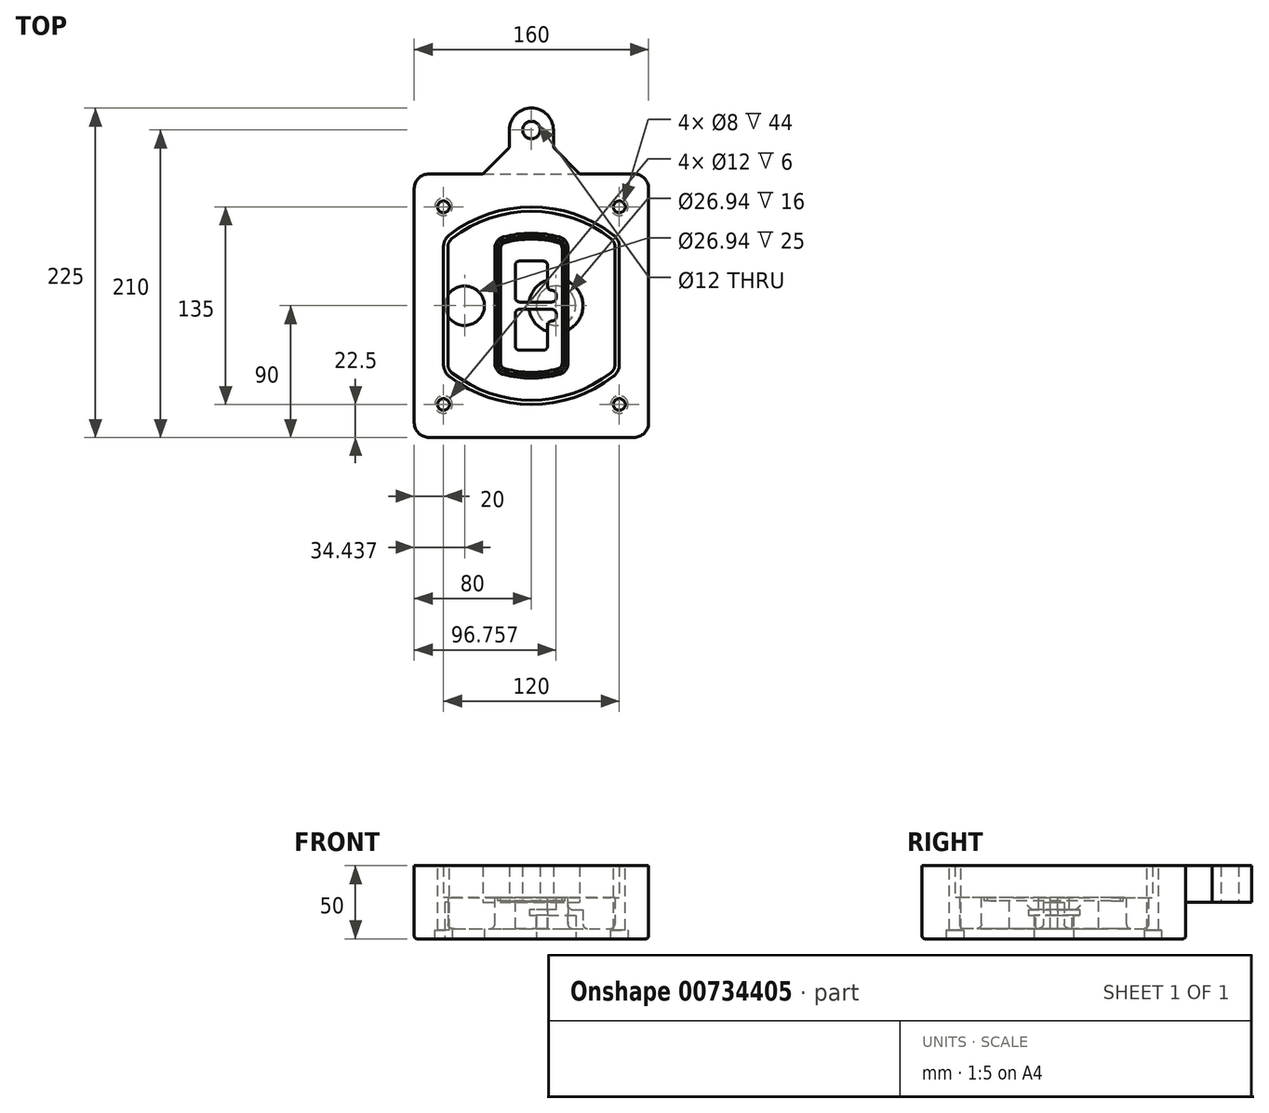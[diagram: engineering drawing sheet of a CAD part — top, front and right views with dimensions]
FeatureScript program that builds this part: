
annotation { "Feature Type Name" : "Feature", "Feature Type Description" : "" }
export const myFeature = defineFeature(function(context is Context, id is Id, definition is map)
    precondition{}
    {
        {
            var Q0;
            Q0=qCreatedBy(makeId("Top.planeOp"),FACE);
            var sketch = newSketch(context, id + "F0", { "sketchPlane" : qUnion([Q0])});
            skPoint(sketch, "E0.rect.middle", {"position": v(0, 0) * mm});
            skLineSegment(sketch, "E1.bottom", {"start": v(-70, -90) * mm, "end": v(70, -90) * mm});
            skLineSegment(sketch, "E1.top", {"start": v(-70, 90) * mm, "end": v(70, 90) * mm});
            skLineSegment(sketch, "E1.left", {"start": v(-80, -80) * mm, "end": v(-80, 80) * mm});
            skLineSegment(sketch, "E1.right", {"start": v(80, -80) * mm, "end": v(80, 80) * mm});
            skLineSegment(sketch, "E2", {"start": v(-80, 90) * mm, "end": v(80, -90) * mm, "construction": true});
            skLineSegment(sketch, "E3", {"start": v(80, 90) * mm, "end": v(-80, -90) * mm, "construction": true});
            skCircle(sketch, "E4", {"center": v(-60, 67.5) * mm, "radius": 4 * mm});
            skCircle(sketch, "E5", {"center": v(60, 67.5) * mm, "radius": 4 * mm});
            skCircle(sketch, "E6", {"center": v(60, -67.5) * mm, "radius": 4 * mm});
            skCircle(sketch, "E7", {"center": v(-60, -67.5) * mm, "radius": 4 * mm});
            skLineSegment(sketch, "E8", {"start": v(-60, 67.5) * mm, "end": v(60, 67.5) * mm, "construction": true});
            skLineSegment(sketch, "E9", {"start": v(60, 67.5) * mm, "end": v(60, -67.5) * mm, "construction": true});
            skLineSegment(sketch, "E10", {"start": v(60, -67.5) * mm, "end": v(-60, -67.5) * mm, "construction": true});
            skLineSegment(sketch, "E11", {"start": v(-60, -67.5) * mm, "end": v(-60, 67.5) * mm, "construction": true});
            skLineSegment(sketch, "E12", {"start": v(-60, 40.3) * mm, "end": v(-60, -40.3) * mm});
            skLineSegment(sketch, "E13", {"start": v(60, 40.3) * mm, "end": v(60, -40.3) * mm});
            skArc(sketch, "E14", {"start": v(56.15, 48.18) * mm, "mid": v(0, 67.5) * mm, "end": v(-56.15, 48.18) * mm});
            skArc(sketch, "E15", {"start": v(-56.15, -48.18) * mm, "mid": v(0, -67.5) * mm, "end": v(56.15, -48.18) * mm});
            skLineSegment(sketch, "E16", {"start": v(-60, 0) * mm, "end": v(60, 0) * mm, "construction": true});
            skPoint(sketch, "E17.visualSharp", {"position": v(-60, -45) * mm});
            skArc(sketch, "E17.filletArc", {"start": v(-60, -40.3) * mm, "mid": v(-58.99, -44.68) * mm, "end": v(-56.15, -48.18) * mm});
            skPoint(sketch, "E18.visualSharp", {"position": v(-60, 45) * mm});
            skArc(sketch, "E18.filletArc", {"start": v(-56.15, 48.18) * mm, "mid": v(-58.99, 44.68) * mm, "end": v(-60, 40.3) * mm});
            skPoint(sketch, "E19.visualSharp", {"position": v(60, 45) * mm});
            skArc(sketch, "E19.filletArc", {"start": v(60, 40.3) * mm, "mid": v(58.99, 44.68) * mm, "end": v(56.15, 48.18) * mm});
            skPoint(sketch, "E20.visualSharp", {"position": v(60, -45) * mm});
            skArc(sketch, "E20.filletArc", {"start": v(56.15, -48.18) * mm, "mid": v(58.99, -44.68) * mm, "end": v(60, -40.3) * mm});
            skPoint(sketch, "E21.visualSharp", {"position": v(-80, 90) * mm});
            skArc(sketch, "E21.filletArc", {"start": v(-70, 90) * mm, "mid": v(-77.07, 87.07) * mm, "end": v(-80, 80) * mm});
            skPoint(sketch, "E22.visualSharp", {"position": v(80, 90) * mm});
            skArc(sketch, "E22.filletArc", {"start": v(80, 80) * mm, "mid": v(77.07, 87.07) * mm, "end": v(70, 90) * mm});
            skPoint(sketch, "E23.visualSharp", {"position": v(80, -90) * mm});
            skArc(sketch, "E23.filletArc", {"start": v(70, -90) * mm, "mid": v(77.07, -87.07) * mm, "end": v(80, -80) * mm});
            skPoint(sketch, "E24.visualSharp", {"position": v(-80, -90) * mm});
            skArc(sketch, "E24.filletArc", {"start": v(-80, -80) * mm, "mid": v(-77.07, -87.07) * mm, "end": v(-70, -90) * mm});
            skArc(sketch, "E25.0", {"start": v(57, 40.3) * mm, "mid": v(56.3, 43.36) * mm, "end": v(54.3, 45.81) * mm});
            skLineSegment(sketch, "E25.1", {"start": v(57, 40.3) * mm, "end": v(57, -40.3) * mm});
            skArc(sketch, "E25.2", {"start": v(54.3, -45.81) * mm, "mid": v(56.3, -43.36) * mm, "end": v(57, -40.3) * mm});
            skArc(sketch, "E25.3", {"start": v(-54.3, -45.81) * mm, "mid": v(0, -64.5) * mm, "end": v(54.3, -45.81) * mm});
            skArc(sketch, "E25.4", {"start": v(-57, -40.3) * mm, "mid": v(-56.3, -43.36) * mm, "end": v(-54.3, -45.81) * mm});
            skArc(sketch, "E25.5", {"start": v(54.3, 45.81) * mm, "mid": v(0, 64.5) * mm, "end": v(-54.3, 45.81) * mm});
            skLineSegment(sketch, "E25.6", {"start": v(-57, 40.3) * mm, "end": v(-57, -40.3) * mm});
            skArc(sketch, "E25.7", {"start": v(-54.3, 45.81) * mm, "mid": v(-56.3, 43.36) * mm, "end": v(-57, 40.3) * mm});
            skArc(sketch, "E26.0", {"start": v(-58.62, 51.33) * mm, "mid": v(-62.58, 46.43) * mm, "end": v(-64, 40.3) * mm});
            skArc(sketch, "E26.1", {"start": v(58.62, 51.33) * mm, "mid": v(0, 71.5) * mm, "end": v(-58.62, 51.33) * mm});
            skArc(sketch, "E26.2", {"start": v(64, 40.3) * mm, "mid": v(62.58, 46.43) * mm, "end": v(58.62, 51.33) * mm});
            skLineSegment(sketch, "E26.3", {"start": v(64, 40.3) * mm, "end": v(64, -40.3) * mm});
            skArc(sketch, "E26.4", {"start": v(58.62, -51.33) * mm, "mid": v(62.58, -46.43) * mm, "end": v(64, -40.3) * mm});
            skLineSegment(sketch, "E26.5", {"start": v(-64, 40.3) * mm, "end": v(-64, -40.3) * mm});
            skArc(sketch, "E26.6", {"start": v(-58.62, -51.33) * mm, "mid": v(0, -71.5) * mm, "end": v(58.62, -51.33) * mm});
            skArc(sketch, "E26.7", {"start": v(-64, -40.3) * mm, "mid": v(-62.58, -46.43) * mm, "end": v(-58.62, -51.33) * mm});
            skSolve(sketch);
        }
        {
            var Q0;
            Q0=makeQuery(id+"F0.imprint","IMPRINT",FACE,{"disambiguationData":[TD([[makeQuery(id+"F0.imprint","IMPRINT",EDGE,{"derivedFrom":sQuery(id+"F0.wireOp",EDGE,"E1.bottom")}),1.0]])]});
            var Q1;
            Q1=makeQuery(id+"F0.imprint","IMPRINT",FACE,{"disambiguationData":[TD([[makeQuery(id+"F0.imprint","IMPRINT",EDGE,{"derivedFrom":sQuery(id+"F0.wireOp",EDGE,"E12")}),1.0]])]});
            var Q2;
            Q2=makeQuery(id+"F0.imprint","IMPRINT",FACE,{"disambiguationData":[TD([[makeQuery(id+"F0.imprint","IMPRINT",EDGE,{"derivedFrom":sQuery(id+"F0.wireOp",EDGE,"E25.0")}),1.0]])]});
            var Q3;
            Q3=makeQuery(id+"F0.imprint","IMPRINT",FACE,{"disambiguationData":[TD([[makeQuery(id+"F0.imprint","IMPRINT",EDGE,{"derivedFrom":sQuery(id+"F0.wireOp",EDGE,"E12")}),-1.0]])]});
            extrude(context, id + "F1", {"entities" : qUnion([Q0, Q1, Q2, Q3]), "oppositeDirection" : true, "depth" : 25 * mm});
        }
        {
            var Q0;
            Q0=makeQuery(id+"F0.imprint","IMPRINT",FACE,{"disambiguationData":[TD([[makeQuery(id+"F0.imprint","IMPRINT",EDGE,{"derivedFrom":sQuery(id+"F0.wireOp",EDGE,"E12")}),1.0]])]});
            extrude(context, id + "F2", {"entities" : qUnion([Q0]), "operationType" : NewBodyOperationType.ADD, "depth" : 3 * mm});
        }
        {
            var Q0;
            Q0=makeQuery(id+"F0.imprint","IMPRINT",FACE,{"disambiguationData":[TD([[makeQuery(id+"F0.imprint","IMPRINT",EDGE,{"derivedFrom":sQuery(id+"F0.wireOp",EDGE,"E25.0")}),1.0]])]});
            extrude(context, id + "F3", {"entities" : qUnion([Q0]), "operationType" : NewBodyOperationType.REMOVE, "oppositeDirection" : true, "depth" : 18 * mm});
        }
        {
            var Q0;
            Q0=makeQuery(id+"F2.opExtrude","CAP_FACE",FACE,{"disambiguationData":[OSD([sQuery(id+"F0.wireOp",EDGE,"E12"),sQuery(id+"F0.wireOp",EDGE,"E13"),sQuery(id+"F0.wireOp",EDGE,"E14"),sQuery(id+"F0.wireOp",EDGE,"E15"),sQuery(id+"F0.wireOp",EDGE,"E17.filletArc"),sQuery(id+"F0.wireOp",EDGE,"E18.filletArc"),sQuery(id+"F0.wireOp",EDGE,"E19.filletArc"),sQuery(id+"F0.wireOp",EDGE,"E20.filletArc"),sQuery(id+"F0.wireOp",EDGE,"E25.0"),sQuery(id+"F0.wireOp",EDGE,"E25.1"),sQuery(id+"F0.wireOp",EDGE,"E25.2"),sQuery(id+"F0.wireOp",EDGE,"E25.3"),sQuery(id+"F0.wireOp",EDGE,"E25.4"),sQuery(id+"F0.wireOp",EDGE,"E25.5"),sQuery(id+"F0.wireOp",EDGE,"E25.6"),sQuery(id+"F0.wireOp",EDGE,"E25.7")])],"isStart":false});
            var sketch = newSketch(context, id + "F4", { "sketchPlane" : qUnion([Q0])});
            skArc(sketch, "E27.0", {"start": v(-19.08, -46.97) * mm, "mid": v(0, -49.5) * mm, "end": v(19.08, -46.97) * mm});
            skArc(sketch, "E28.0", {"start": v(19.08, 46.97) * mm, "mid": v(0, 49.5) * mm, "end": v(-19.08, 46.97) * mm});
            skLineSegment(sketch, "E29", {"start": v(-25, 39.25) * mm, "end": v(-25, -39.25) * mm});
            skLineSegment(sketch, "E30", {"start": v(25, 39.25) * mm, "end": v(25, -39.25) * mm});
            skLineSegment(sketch, "E31", {"start": v(-25, 45.1) * mm, "end": v(25, 45.1) * mm, "construction": true});
            skLineSegment(sketch, "E32", {"start": v(-25, -45.1) * mm, "end": v(25, -45.1) * mm, "construction": true});
            skPoint(sketch, "E33.visualSharp", {"position": v(-25, 45.1) * mm});
            skArc(sketch, "E33.filletArc", {"start": v(-19.08, 46.97) * mm, "mid": v(-23.35, 44.11) * mm, "end": v(-25, 39.25) * mm});
            skPoint(sketch, "E34.visualSharp", {"position": v(25, 45.1) * mm});
            skArc(sketch, "E34.filletArc", {"start": v(25, 39.25) * mm, "mid": v(23.35, 44.11) * mm, "end": v(19.08, 46.97) * mm});
            skPoint(sketch, "E35.visualSharp", {"position": v(25, -45.1) * mm});
            skArc(sketch, "E35.filletArc", {"start": v(19.08, -46.97) * mm, "mid": v(23.35, -44.11) * mm, "end": v(25, -39.25) * mm});
            skPoint(sketch, "E36.visualSharp", {"position": v(-25, -45.1) * mm});
            skArc(sketch, "E36.filletArc", {"start": v(-25, -39.25) * mm, "mid": v(-23.35, -44.11) * mm, "end": v(-19.08, -46.97) * mm});
            skArc(sketch, "E37.0", {"start": v(54.3, 45.81) * mm, "mid": v(0, 64.5) * mm, "end": v(-54.3, 45.81) * mm});
            skArc(sketch, "E37.1", {"start": v(-54.3, 45.81) * mm, "mid": v(-56.3, 43.36) * mm, "end": v(-57, 40.3) * mm});
            skLineSegment(sketch, "E37.2", {"start": v(-57, 40.3) * mm, "end": v(-57, -40.3) * mm});
            skArc(sketch, "E37.3", {"start": v(-57, -40.3) * mm, "mid": v(-56.3, -43.36) * mm, "end": v(-54.3, -45.81) * mm});
            skArc(sketch, "E37.4", {"start": v(-54.3, -45.81) * mm, "mid": v(0, -64.5) * mm, "end": v(54.3, -45.81) * mm});
            skArc(sketch, "E37.5", {"start": v(54.3, -45.81) * mm, "mid": v(56.3, -43.36) * mm, "end": v(57, -40.3) * mm});
            skLineSegment(sketch, "E37.6", {"start": v(57, 40.3) * mm, "end": v(57, -40.3) * mm});
            skArc(sketch, "E37.7", {"start": v(57, 40.3) * mm, "mid": v(56.3, 43.36) * mm, "end": v(54.3, 45.81) * mm});
            skLineSegment(sketch, "E38.0", {"start": v(23, 39.25) * mm, "end": v(23, -39.25) * mm});
            skArc(sketch, "E38.1", {"start": v(18.56, -45.04) * mm, "mid": v(21.76, -42.9) * mm, "end": v(23, -39.25) * mm});
            skArc(sketch, "E38.2", {"start": v(-18.56, -45.04) * mm, "mid": v(0, -47.5) * mm, "end": v(18.56, -45.04) * mm});
            skArc(sketch, "E38.3", {"start": v(-23, -39.25) * mm, "mid": v(-21.76, -42.9) * mm, "end": v(-18.56, -45.04) * mm});
            skLineSegment(sketch, "E38.4", {"start": v(-23, 39.25) * mm, "end": v(-23, -39.25) * mm});
            skArc(sketch, "E38.5", {"start": v(23, 39.25) * mm, "mid": v(21.76, 42.9) * mm, "end": v(18.56, 45.04) * mm});
            skArc(sketch, "E38.6", {"start": v(-18.56, 45.04) * mm, "mid": v(-21.76, 42.9) * mm, "end": v(-23, 39.25) * mm});
            skArc(sketch, "E38.7", {"start": v(18.56, 45.04) * mm, "mid": v(0, 47.5) * mm, "end": v(-18.56, 45.04) * mm});
            skArc(sketch, "E39.0", {"start": v(21, 39.25) * mm, "mid": v(20.18, 41.68) * mm, "end": v(18.04, 43.1) * mm});
            skLineSegment(sketch, "E39.1", {"start": v(21, 39.25) * mm, "end": v(21, -39.25) * mm});
            skArc(sketch, "E39.2", {"start": v(18.04, -43.1) * mm, "mid": v(20.18, -41.68) * mm, "end": v(21, -39.25) * mm});
            skArc(sketch, "E39.3", {"start": v(-18.04, -43.1) * mm, "mid": v(0, -45.5) * mm, "end": v(18.04, -43.1) * mm});
            skArc(sketch, "E39.4", {"start": v(-21, -39.25) * mm, "mid": v(-20.18, -41.68) * mm, "end": v(-18.04, -43.1) * mm});
            skArc(sketch, "E39.5", {"start": v(18.04, 43.1) * mm, "mid": v(0, 45.5) * mm, "end": v(-18.04, 43.1) * mm});
            skLineSegment(sketch, "E39.6", {"start": v(-21, 39.25) * mm, "end": v(-21, -39.25) * mm});
            skArc(sketch, "E39.7", {"start": v(-18.04, 43.1) * mm, "mid": v(-20.18, 41.68) * mm, "end": v(-21, 39.25) * mm});
            skLineSegment(sketch, "E40", {"start": v(-25, 0) * mm, "end": v(25, 0) * mm, "construction": true});
            skLineSegment(sketch, "E41", {"start": v(-11, 5.5) * mm, "end": v(-11, 27.5) * mm});
            skLineSegment(sketch, "E42", {"start": v(-8, 30.5) * mm, "end": v(8, 30.5) * mm});
            skLineSegment(sketch, "E43", {"start": v(11, 27.5) * mm, "end": v(11, 13.5) * mm});
            skLineSegment(sketch, "E44", {"start": v(14, 10.5) * mm, "end": v(14, 10.5) * mm});
            skLineSegment(sketch, "E45", {"start": v(17, 7.5) * mm, "end": v(17, 5.5) * mm});
            skLineSegment(sketch, "E46", {"start": v(14, 2.5) * mm, "end": v(-8, 2.5) * mm});
            skPoint(sketch, "E47.visualSharp", {"position": v(-11, 30.5) * mm});
            skArc(sketch, "E47.filletArc", {"start": v(-8, 30.5) * mm, "mid": v(-10.12, 29.62) * mm, "end": v(-11, 27.5) * mm});
            skPoint(sketch, "E48.visualSharp", {"position": v(11, 30.5) * mm});
            skArc(sketch, "E48.filletArc", {"start": v(11, 27.5) * mm, "mid": v(10.12, 29.62) * mm, "end": v(8, 30.5) * mm});
            skPoint(sketch, "E49.visualSharp", {"position": v(11, 10.5) * mm});
            skArc(sketch, "E49.filletArc", {"start": v(11, 13.5) * mm, "mid": v(11.88, 11.38) * mm, "end": v(14, 10.5) * mm});
            skPoint(sketch, "E50.visualSharp", {"position": v(17, 10.5) * mm});
            skArc(sketch, "E50.filletArc", {"start": v(17, 7.5) * mm, "mid": v(16.12, 9.62) * mm, "end": v(14, 10.5) * mm});
            skPoint(sketch, "E51.visualSharp", {"position": v(17, 2.5) * mm});
            skArc(sketch, "E51.filletArc", {"start": v(14, 2.5) * mm, "mid": v(16.12, 3.38) * mm, "end": v(17, 5.5) * mm});
            skPoint(sketch, "E52.visualSharp", {"position": v(-11, 2.5) * mm});
            skArc(sketch, "E52.filletArc", {"start": v(-11, 5.5) * mm, "mid": v(-10.12, 3.38) * mm, "end": v(-8, 2.5) * mm});
            skLineSegment(sketch, "E53.0.MirrorCS", {"start": v(14, -2.5) * mm, "end": v(-8, -2.5) * mm});
            skArc(sketch, "E54.0.MirrorCS", {"start": v(-11, -5.5) * mm, "mid": v(-10.12, -3.38) * mm, "end": v(-8, -2.5) * mm});
            skLineSegment(sketch, "E55.0.MirrorCS", {"start": v(-11, -5.5) * mm, "end": v(-11, -27.5) * mm});
            skArc(sketch, "E56.0.MirrorCS", {"start": v(-8, -30.5) * mm, "mid": v(-10.12, -29.62) * mm, "end": v(-11, -27.5) * mm});
            skLineSegment(sketch, "E57.0.MirrorCS", {"start": v(-8, -30.5) * mm, "end": v(8, -30.5) * mm});
            skArc(sketch, "E58.0.MirrorCS", {"start": v(11, -27.5) * mm, "mid": v(10.12, -29.62) * mm, "end": v(8, -30.5) * mm});
            skLineSegment(sketch, "E59.0.MirrorCS", {"start": v(11, -27.5) * mm, "end": v(11, -13.5) * mm});
            skArc(sketch, "E60.0.MirrorCS", {"start": v(11, -13.5) * mm, "mid": v(11.88, -11.38) * mm, "end": v(14, -10.5) * mm});
            skArc(sketch, "E61.0.MirrorCS", {"start": v(17, -7.5) * mm, "mid": v(16.12, -9.62) * mm, "end": v(14, -10.5) * mm});
            skLineSegment(sketch, "E62.0.MirrorCS", {"start": v(17, -7.5) * mm, "end": v(17, -5.5) * mm});
            skArc(sketch, "E63.0.MirrorCS", {"start": v(14, -2.5) * mm, "mid": v(16.12, -3.38) * mm, "end": v(17, -5.5) * mm});
            skSolve(sketch);
        }
        {
            var Q0;
            Q0=makeQuery(id+"F4.imprint","IMPRINT",FACE,{"disambiguationData":[TD([[makeQuery(id+"F4.imprint","IMPRINT",EDGE,{"derivedFrom":sQuery(id+"F4.wireOp",EDGE,"E27.0")}),1.0]])]});
            var Q1;
            Q1=makeQuery(id+"F4.imprint","IMPRINT",FACE,{"disambiguationData":[TD([[makeQuery(id+"F4.imprint","IMPRINT",EDGE,{"derivedFrom":sQuery(id+"F4.wireOp",EDGE,"E38.0")}),-1.0]])]});
            var Q2;
            Q2=makeQuery(id+"F4.imprint","IMPRINT",FACE,{"disambiguationData":[TD([[makeQuery(id+"F4.imprint","IMPRINT",EDGE,{"derivedFrom":sQuery(id+"F4.wireOp",EDGE,"E39.0")}),1.0]])]});
            extrude(context, id + "F5", {"entities" : qUnion([Q0, Q1, Q2]), "operationType" : NewBodyOperationType.ADD, "endBound" : BoundingType.UP_TO_NEXT, "oppositeDirection" : true, "depth" : 25 * mm});
        }
        {
            var Q0;
            Q0=makeQuery(id+"F4.imprint","IMPRINT",FACE,{"disambiguationData":[TD([[makeQuery(id+"F4.imprint","IMPRINT",EDGE,{"derivedFrom":sQuery(id+"F4.wireOp",EDGE,"E38.0")}),-1.0]])]});
            extrude(context, id + "F6", {"entities" : qUnion([Q0]), "operationType" : NewBodyOperationType.REMOVE, "oppositeDirection" : true, "depth" : 2 * mm});
        }
        {
            var Q0;
            Q0=makeQuery(id+"F1.opExtrude","CAP_FACE",FACE,{"disambiguationData":[OSD([sQuery(id+"F0.wireOp",EDGE,"E1.bottom"),sQuery(id+"F0.wireOp",EDGE,"E1.top"),sQuery(id+"F0.wireOp",EDGE,"E1.left"),sQuery(id+"F0.wireOp",EDGE,"E1.right"),sQuery(id+"F0.wireOp",EDGE,"E4"),sQuery(id+"F0.wireOp",EDGE,"E5"),sQuery(id+"F0.wireOp",EDGE,"E6"),sQuery(id+"F0.wireOp",EDGE,"E7"),sQuery(id+"F0.wireOp",EDGE,"E21.filletArc"),sQuery(id+"F0.wireOp",EDGE,"E22.filletArc"),sQuery(id+"F0.wireOp",EDGE,"E23.filletArc"),sQuery(id+"F0.wireOp",EDGE,"E24.filletArc")])],"isStart":false});
            var sketch = newSketch(context, id + "F7", { "sketchPlane" : qUnion([Q0])});
            skCircle(sketch, "E64", {"center": v(16.76, 0) * mm, "radius": 13.47 * mm});
            skCircle(sketch, "E65", {"center": v(-45.56, 0) * mm, "radius": 13.47 * mm});
            skLineSegment(sketch, "E66", {"start": v(80, 0) * mm, "end": v(-80, 0) * mm});
            skCircle(sketch, "E67", {"center": v(16.76, 0) * mm, "radius": 18.47 * mm});
            skCircle(sketch, "E68", {"center": v(60, -67.5) * mm, "radius": 6 * mm});
            skCircle(sketch, "E69", {"center": v(-60, -67.5) * mm, "radius": 6 * mm});
            skCircle(sketch, "E70", {"center": v(-60, 67.5) * mm, "radius": 6 * mm});
            skCircle(sketch, "E71", {"center": v(60, 67.5) * mm, "radius": 6 * mm});
            skSolve(sketch);
        }
        {
            var Q0;
            {var subQ1=sQuery(id+"F7.wireOp",EDGE,"E66");var subQ4=sQuery(id+"F7.wireOp",EDGE,"E64");var subQ6=makeQuery(id+"F7.imprint","INTERSECT",VERTEX,{"disambiguationData":[OD(0.0)],"derivedFrom":[subQ4,subQ1]});Q0=makeQuery(id+"F7.imprint","IMPRINT",FACE,{"disambiguationData":[TD([[makeQuery(id+"F7.imprint","IMPRINT",EDGE,{"disambiguationData":[TD([[subQ6,-1.0]])],"derivedFrom":subQ4}),-1.0]])]});}
            var Q1;
            {var subQ0=sQuery(id+"F7.wireOp",EDGE,"E66");var subQ1=sQuery(id+"F7.wireOp",EDGE,"E64");var subQ3=makeQuery(id+"F7.imprint","INTERSECT",VERTEX,{"disambiguationData":[OD(0.0)],"derivedFrom":[subQ1,subQ0]});Q1=makeQuery(id+"F7.imprint","IMPRINT",FACE,{"disambiguationData":[TD([[makeQuery(id+"F7.imprint","IMPRINT",EDGE,{"disambiguationData":[TD([[subQ3,-1.0]])],"derivedFrom":subQ1}),1.0]])]});}
            var Q2;
            {var subQ0=sQuery(id+"F7.wireOp",EDGE,"E66");var subQ1=sQuery(id+"F7.wireOp",EDGE,"E64");var subQ3=makeQuery(id+"F7.imprint","INTERSECT",VERTEX,{"disambiguationData":[OD(0.0)],"derivedFrom":[subQ1,subQ0]});Q2=makeQuery(id+"F7.imprint","IMPRINT",FACE,{"disambiguationData":[TD([[makeQuery(id+"F7.imprint","IMPRINT",EDGE,{"disambiguationData":[TD([[subQ3,1.0]])],"derivedFrom":subQ1}),1.0]])]});}
            var Q3;
            {var subQ1=sQuery(id+"F7.wireOp",EDGE,"E66");var subQ4=sQuery(id+"F7.wireOp",EDGE,"E64");var subQ6=makeQuery(id+"F7.imprint","INTERSECT",VERTEX,{"disambiguationData":[OD(0.0)],"derivedFrom":[subQ4,subQ1]});Q3=makeQuery(id+"F7.imprint","IMPRINT",FACE,{"disambiguationData":[TD([[makeQuery(id+"F7.imprint","IMPRINT",EDGE,{"disambiguationData":[TD([[subQ6,1.0]])],"derivedFrom":subQ4}),-1.0]])]});}
            extrude(context, id + "F8", {"entities" : qUnion([Q0, Q1, Q2, Q3]), "operationType" : NewBodyOperationType.ADD, "oppositeDirection" : true, "depth" : 20 * mm});
        }
        {
            var Q0;
            {var subQ0=sQuery(id+"F7.wireOp",EDGE,"E66");var subQ1=sQuery(id+"F7.wireOp",EDGE,"E64");var subQ3=makeQuery(id+"F7.imprint","INTERSECT",VERTEX,{"disambiguationData":[OD(0.0)],"derivedFrom":[subQ1,subQ0]});Q0=makeQuery(id+"F7.imprint","IMPRINT",FACE,{"disambiguationData":[TD([[makeQuery(id+"F7.imprint","IMPRINT",EDGE,{"disambiguationData":[TD([[subQ3,-1.0]])],"derivedFrom":subQ1}),1.0]])]});}
            var Q1;
            {var subQ0=sQuery(id+"F7.wireOp",EDGE,"E66");var subQ1=sQuery(id+"F7.wireOp",EDGE,"E64");var subQ3=makeQuery(id+"F7.imprint","INTERSECT",VERTEX,{"disambiguationData":[OD(0.0)],"derivedFrom":[subQ1,subQ0]});Q1=makeQuery(id+"F7.imprint","IMPRINT",FACE,{"disambiguationData":[TD([[makeQuery(id+"F7.imprint","IMPRINT",EDGE,{"disambiguationData":[TD([[subQ3,1.0]])],"derivedFrom":subQ1}),1.0]])]});}
            extrude(context, id + "F9", {"entities" : qUnion([Q0, Q1]), "operationType" : NewBodyOperationType.REMOVE, "oppositeDirection" : true, "depth" : 16 * mm});
        }
        {
            var Q0;
            {var subQ0=sQuery(id+"F7.wireOp",EDGE,"E66");var subQ1=sQuery(id+"F7.wireOp",EDGE,"E65");var subQ3=makeQuery(id+"F7.imprint","INTERSECT",VERTEX,{"disambiguationData":[OD(0.0)],"derivedFrom":[subQ1,subQ0]});Q0=makeQuery(id+"F7.imprint","IMPRINT",FACE,{"disambiguationData":[TD([[makeQuery(id+"F7.imprint","IMPRINT",EDGE,{"disambiguationData":[TD([[subQ3,-1.0]])],"derivedFrom":subQ1}),1.0]])]});}
            var Q1;
            {var subQ0=sQuery(id+"F7.wireOp",EDGE,"E66");var subQ1=sQuery(id+"F7.wireOp",EDGE,"E65");var subQ3=makeQuery(id+"F7.imprint","INTERSECT",VERTEX,{"disambiguationData":[OD(0.0)],"derivedFrom":[subQ1,subQ0]});Q1=makeQuery(id+"F7.imprint","IMPRINT",FACE,{"disambiguationData":[TD([[makeQuery(id+"F7.imprint","IMPRINT",EDGE,{"disambiguationData":[TD([[subQ3,1.0]])],"derivedFrom":subQ1}),1.0]])]});}
            extrude(context, id + "F10", {"entities" : qUnion([Q0, Q1]), "operationType" : NewBodyOperationType.REMOVE, "oppositeDirection" : true, "depth" : 25 * mm});
        }
        {
            var Q0;
            Q0=makeQuery(id+"F7.imprint","IMPRINT",FACE,{"disambiguationData":[TD([[makeQuery(id+"F7.imprint","IMPRINT",EDGE,{"derivedFrom":sQuery(id+"F7.wireOp",EDGE,"E68")}),1.0]])]});
            var Q1;
            Q1=makeQuery(id+"F7.imprint","IMPRINT",FACE,{"disambiguationData":[TD([[makeQuery(id+"F7.imprint","IMPRINT",EDGE,{"derivedFrom":makeQuery(id+"F1.opExtrude","CAP_EDGE",EDGE,{"disambiguationData":[OSD([sQuery(id+"F0.wireOp",EDGE,"E5")])],"isStart":false})}),-1.0]])]});
            var Q2;
            Q2=makeQuery(id+"F7.imprint","IMPRINT",FACE,{"disambiguationData":[TD([[makeQuery(id+"F7.imprint","IMPRINT",EDGE,{"derivedFrom":sQuery(id+"F7.wireOp",EDGE,"E69")}),1.0]])]});
            var Q3;
            Q3=makeQuery(id+"F7.imprint","IMPRINT",FACE,{"disambiguationData":[TD([[makeQuery(id+"F7.imprint","IMPRINT",EDGE,{"derivedFrom":makeQuery(id+"F1.opExtrude","CAP_EDGE",EDGE,{"disambiguationData":[OSD([sQuery(id+"F0.wireOp",EDGE,"E4")])],"isStart":false})}),-1.0]])]});
            var Q4;
            Q4=makeQuery(id+"F7.imprint","IMPRINT",FACE,{"disambiguationData":[TD([[makeQuery(id+"F7.imprint","IMPRINT",EDGE,{"derivedFrom":sQuery(id+"F7.wireOp",EDGE,"E70")}),1.0]])]});
            var Q5;
            Q5=makeQuery(id+"F7.imprint","IMPRINT",FACE,{"disambiguationData":[TD([[makeQuery(id+"F7.imprint","IMPRINT",EDGE,{"derivedFrom":makeQuery(id+"F1.opExtrude","CAP_EDGE",EDGE,{"disambiguationData":[OSD([sQuery(id+"F0.wireOp",EDGE,"E7")])],"isStart":false})}),-1.0]])]});
            var Q6;
            Q6=makeQuery(id+"F7.imprint","IMPRINT",FACE,{"disambiguationData":[TD([[makeQuery(id+"F7.imprint","IMPRINT",EDGE,{"derivedFrom":sQuery(id+"F7.wireOp",EDGE,"E71")}),1.0]])]});
            var Q7;
            Q7=makeQuery(id+"F7.imprint","IMPRINT",FACE,{"disambiguationData":[TD([[makeQuery(id+"F7.imprint","IMPRINT",EDGE,{"derivedFrom":makeQuery(id+"F1.opExtrude","CAP_EDGE",EDGE,{"disambiguationData":[OSD([sQuery(id+"F0.wireOp",EDGE,"E6")])],"isStart":false})}),-1.0]])]});
            extrude(context, id + "F11", {"entities" : qUnion([Q0, Q1, Q2, Q3, Q4, Q5, Q6, Q7]), "operationType" : NewBodyOperationType.REMOVE, "oppositeDirection" : true, "depth" : 6 * mm});
        }
        {
            var Q0;
            Q0=makeQuery(id+"F9.boolean.opBoolean","COPY",FACE,{"derivedFrom":makeQuery(id+"F9.opExtrude","CAP_FACE",FACE,{"disambiguationData":[OSD([sQuery(id+"F7.wireOp",EDGE,"E64")])],"isStart":false})});
            var sketch = newSketch(context, id + "F12", { "sketchPlane" : qUnion([Q0])});
            skArc(sketch, "E72.0", {"start": v(11, 17.55) * mm, "mid": v(2.57, 11.82) * mm, "end": v(-1.54, 2.5) * mm});
            skArc(sketch, "E72.1", {"start": v(-1.54, -2.5) * mm, "mid": v(2.57, -11.82) * mm, "end": v(11, -17.55) * mm});
            skLineSegment(sketch, "E73", {"start": v(-1.54, -2.5) * mm, "end": v(14, -2.5) * mm});
            skLineSegment(sketch, "E74.0", {"start": v(14, 2.5) * mm, "end": v(-1.54, 2.5) * mm});
            skArc(sketch, "E74.1", {"start": v(14, 2.5) * mm, "mid": v(16.12, 3.38) * mm, "end": v(17, 5.5) * mm});
            skLineSegment(sketch, "E74.2", {"start": v(17, 7.5) * mm, "end": v(17, 5.5) * mm});
            skArc(sketch, "E74.3", {"start": v(17, 7.5) * mm, "mid": v(16.12, 9.62) * mm, "end": v(14, 10.5) * mm});
            skArc(sketch, "E74.4", {"start": v(11, 13.5) * mm, "mid": v(11.88, 11.38) * mm, "end": v(14, 10.5) * mm});
            skLineSegment(sketch, "E74.5", {"start": v(11, 17.55) * mm, "end": v(11, 13.5) * mm});
            skLineSegment(sketch, "E74.7", {"start": v(14, -2.5) * mm, "end": v(-1.54, -2.5) * mm});
            skArc(sketch, "E74.8", {"start": v(14, -2.5) * mm, "mid": v(16.12, -3.38) * mm, "end": v(17, -5.5) * mm});
            skLineSegment(sketch, "E74.9", {"start": v(17, -7.5) * mm, "end": v(17, -5.5) * mm});
            skArc(sketch, "E74.10", {"start": v(17, -7.5) * mm, "mid": v(16.12, -9.62) * mm, "end": v(14, -10.5) * mm});
            skArc(sketch, "E74.11", {"start": v(11, -13.5) * mm, "mid": v(11.88, -11.38) * mm, "end": v(14, -10.5) * mm});
            skLineSegment(sketch, "E74.12", {"start": v(11, -17.55) * mm, "end": v(11, -13.5) * mm});
            skPoint(sketch, "E75.orphan", {"position": v(11, -27.5) * mm});
            skPoint(sketch, "E76.orphan", {"position": v(-8, -2.5) * mm});
            skPoint(sketch, "E77.orphan", {"position": v(-8, 2.5) * mm});
            skPoint(sketch, "E78.orphan", {"position": v(11, 27.5) * mm});
            skSolve(sketch);
        }
        {
            var Q0;
            {var subQ7=sQuery(id+"F12.wireOp",EDGE,"E72.0");var subQ14=sQuery(id+"F12.wireOp",EDGE,"E72.1");var subQ16=sQuery(id+"F12.wireOp",EDGE,"E74.1");var subQ18=sQuery(id+"F12.wireOp",EDGE,"E74.8");Q0=qUnion([makeQuery(id+"F12.imprint","IMPRINT",FACE,{"disambiguationData":[TD([[makeQuery(id+"F12.imprint","IMPRINT",EDGE,{"derivedFrom":subQ7}),1.0]])]}),makeQuery(id+"F12.imprint","IMPRINT",FACE,{"disambiguationData":[TD([[makeQuery(id+"F12.imprint","IMPRINT",EDGE,{"derivedFrom":subQ14}),1.0]])]}),makeQuery(id+"F12.imprint","IMPRINT",FACE,{"disambiguationData":[TD([[makeQuery(id+"F12.imprint","IMPRINT",EDGE,{"derivedFrom":subQ16}),1.0]])]}),makeQuery(id+"F12.imprint","IMPRINT",FACE,{"disambiguationData":[TD([[makeQuery(id+"F12.imprint","IMPRINT",EDGE,{"derivedFrom":subQ18}),-1.0]])]})]);}
            var Q1;
            Q1=makeQuery(id+"F5.boolean.opBoolean","SPLIT",FACE,{"disambiguationData":[TD([makeQuery(id+"F5.opExtrude","SWEPT_FACE",FACE,{"disambiguationData":[OSD([sQuery(id+"F4.wireOp",EDGE,"E41")])]})])],"derivedFrom":makeQuery(id+"F3.boolean.opBoolean","COPY",FACE,{"derivedFrom":makeQuery(id+"F3.opExtrude","CAP_FACE",FACE,{"disambiguationData":[OSD([sQuery(id+"F0.wireOp",EDGE,"E25.0"),sQuery(id+"F0.wireOp",EDGE,"E25.1"),sQuery(id+"F0.wireOp",EDGE,"E25.2"),sQuery(id+"F0.wireOp",EDGE,"E25.3"),sQuery(id+"F0.wireOp",EDGE,"E25.4"),sQuery(id+"F0.wireOp",EDGE,"E25.5"),sQuery(id+"F0.wireOp",EDGE,"E25.6"),sQuery(id+"F0.wireOp",EDGE,"E25.7")])],"isStart":false})})});
            extrude(context, id + "F13", {"entities" : qUnion([Q0]), "operationType" : NewBodyOperationType.REMOVE, "endBound" : BoundingType.UP_TO_SURFACE, "endBoundEntityFace" : qUnion([Q1]), "depth" : 25 * mm});
        }
        {
            var Q0;
            Q0=makeQuery(id+"F3.boolean.opBoolean","COPY",EDGE,{"derivedFrom":makeQuery(id+"F3.opExtrude","CAP_EDGE",EDGE,{"disambiguationData":[OSD([sQuery(id+"F0.wireOp",EDGE,"E25.6")])],"isStart":false})});
            var Q1;
            Q1=makeQuery(id+"F8.boolean.opBoolean","INTERSECT",EDGE,{"derivedFrom":[makeQuery(id+"F5.opExtrude","SWEPT_FACE",FACE,{"disambiguationData":[OSD([sQuery(id+"F4.wireOp",EDGE,"E30")])]}),makeQuery(id+"F8.opExtrude","CAP_FACE",FACE,{"disambiguationData":[OSD([sQuery(id+"F7.wireOp",EDGE,"E67")])],"isStart":false})]});
            var Q2;
            Q2=makeQuery(id+"F8.boolean.opBoolean","INTERSECT",EDGE,{"disambiguationData":[OD(1.0)],"derivedFrom":[makeQuery(id+"F5.opExtrude","SWEPT_FACE",FACE,{"disambiguationData":[OSD([sQuery(id+"F4.wireOp",EDGE,"E30")])]}),makeQuery(id+"F8.opExtrude","SWEPT_FACE",FACE,{"disambiguationData":[OSD([sQuery(id+"F7.wireOp",EDGE,"E67")])]})]});
            var Q3;
            {var subQ0=sQuery(id+"F4.wireOp",EDGE,"E30");Q3=makeQuery(id+"F8.boolean.opBoolean","SPLIT",EDGE,{"disambiguationData":[TD([makeQuery(id+"F5.opExtrude","SWEPT_FACE",FACE,{"disambiguationData":[OSD([sQuery(id+"F4.wireOp",EDGE,"E35.filletArc")])]})])],"derivedFrom":makeQuery(id+"F5.opExtrude","CAP_EDGE",EDGE,{"disambiguationData":[OSD([subQ0])],"isStart":false})});}
            var Q4;
            {var subQ0=sQuery(id+"F0.wireOp",EDGE,"E25.7");var subQ1=sQuery(id+"F0.wireOp",EDGE,"E25.1");var subQ2=sQuery(id+"F0.wireOp",EDGE,"E25.6");var subQ3=sQuery(id+"F0.wireOp",EDGE,"E25.5");var subQ4=sQuery(id+"F0.wireOp",EDGE,"E25.4");var subQ5=sQuery(id+"F0.wireOp",EDGE,"E25.0");var subQ6=sQuery(id+"F0.wireOp",EDGE,"E25.2");var subQ7=sQuery(id+"F0.wireOp",EDGE,"E25.3");Q4=makeQuery(id+"F8.boolean.opBoolean","INTERSECT",EDGE,{"derivedFrom":[makeQuery(id+"F5.boolean.opBoolean","SPLIT",FACE,{"disambiguationData":[TD([makeQuery(id+"F2.opExtrude","SWEPT_FACE",FACE,{"disambiguationData":[OSD([subQ5])]})])],"derivedFrom":makeQuery(id+"F3.boolean.opBoolean","COPY",FACE,{"derivedFrom":makeQuery(id+"F3.opExtrude","CAP_FACE",FACE,{"disambiguationData":[OSD([subQ5,subQ1,subQ6,subQ7,subQ4,subQ3,subQ2,subQ0])],"isStart":false})})}),makeQuery(id+"F8.opExtrude","SWEPT_FACE",FACE,{"disambiguationData":[OSD([sQuery(id+"F7.wireOp",EDGE,"E67")])]})]});}
            var Q5;
            Q5=makeQuery(id+"F8.boolean.opBoolean","INTERSECT",EDGE,{"disambiguationData":[OD(0.0)],"derivedFrom":[makeQuery(id+"F5.opExtrude","SWEPT_FACE",FACE,{"disambiguationData":[OSD([sQuery(id+"F4.wireOp",EDGE,"E30")])]}),makeQuery(id+"F8.opExtrude","SWEPT_FACE",FACE,{"disambiguationData":[OSD([sQuery(id+"F7.wireOp",EDGE,"E67")])]})]});
            fillet(context, id + "F14", {"entities" : qUnion([Q0, Q1, Q2, Q3, Q4, Q5]), "radius" : 3 * mm, "tangentPropagation" : true, "allowEdgeOverflow" : false});
        }
        {
            var Q0;
            Q0=makeQuery(id+"F1.opExtrude","CAP_EDGE",EDGE,{"disambiguationData":[OSD([sQuery(id+"F0.wireOp",EDGE,"E1.bottom")])],"isStart":false});
            fillet(context, id + "F15", {"entities" : qUnion([Q0]), "radius" : 2 * mm, "tangentPropagation" : true, "allowEdgeOverflow" : false});
        }
        {
            var Q0;
            {var subQ0=sQuery(id+"F0.wireOp",EDGE,"E21.filletArc");var subQ1=sQuery(id+"F0.wireOp",EDGE,"E7");var subQ2=sQuery(id+"F0.wireOp",EDGE,"E6");var subQ3=sQuery(id+"F0.wireOp",EDGE,"E5");var subQ4=sQuery(id+"F0.wireOp",EDGE,"E4");var subQ5=sQuery(id+"F0.wireOp",EDGE,"E22.filletArc");var subQ6=sQuery(id+"F0.wireOp",EDGE,"E1.bottom");var subQ7=sQuery(id+"F0.wireOp",EDGE,"E1.right");var subQ8=sQuery(id+"F0.wireOp",EDGE,"E1.top");var subQ9=sQuery(id+"F0.wireOp",EDGE,"E1.left");var subQ10=sQuery(id+"F0.wireOp",EDGE,"E23.filletArc");var subQ11=sQuery(id+"F0.wireOp",EDGE,"E24.filletArc");Q0=makeQuery(id+"F2.boolean.opBoolean","SPLIT",FACE,{"disambiguationData":[TD([makeQuery(id+"F1.opExtrude","SWEPT_FACE",FACE,{"disambiguationData":[OSD([subQ6])]})])],"derivedFrom":makeQuery(id+"F1.opExtrude","CAP_FACE",FACE,{"disambiguationData":[OSD([subQ6,subQ8,subQ9,subQ7,subQ4,subQ3,subQ2,subQ1,subQ0,subQ5,subQ10,subQ11])],"isStart":true})});}
            var sketch = newSketch(context, id + "F16", { "sketchPlane" : qUnion([Q0])});
            skLineSegment(sketch, "E79", {"start": v(-33, 90) * mm, "end": v(-15, 108) * mm});
            skLineSegment(sketch, "E80", {"start": v(-15, 108) * mm, "end": v(-15, 120) * mm});
            skLineSegment(sketch, "E81", {"start": v(15, 108) * mm, "end": v(15, 120) * mm});
            skArc(sketch, "E82", {"start": v(15, 120) * mm, "mid": v(0, 135) * mm, "end": v(-15, 120) * mm});
            skLineSegment(sketch, "E83", {"start": v(0, 120) * mm, "end": v(0, 90) * mm, "construction": true});
            skCircle(sketch, "E84", {"center": v(0, 120) * mm, "radius": 6 * mm});
            skLineSegment(sketch, "E85", {"start": v(-80, 0) * mm, "end": v(80, 0) * mm, "construction": true});
            skLineSegment(sketch, "E86", {"start": v(15, 108) * mm, "end": v(33, 90) * mm});
            skArc(sketch, "E87.MirrorCS", {"start": v(15, -120) * mm, "mid": v(0, -135) * mm, "end": v(-15, -120) * mm});
            skLineSegment(sketch, "E88.MirrorCS", {"start": v(15, -108) * mm, "end": v(15, -120) * mm});
            skLineSegment(sketch, "E89.MirrorCS", {"start": v(15, -108) * mm, "end": v(33, -90) * mm});
            skLineSegment(sketch, "E90.MirrorCS", {"start": v(0, -120) * mm, "end": v(0, -90) * mm, "construction": true});
            skCircle(sketch, "E91.MirrorC", {"center": v(0, -120) * mm, "radius": 6 * mm});
            skLineSegment(sketch, "E92.MirrorCS", {"start": v(-15, -108) * mm, "end": v(-15, -120) * mm});
            skLineSegment(sketch, "E93.MirrorCS", {"start": v(-33, -90) * mm, "end": v(-15, -108) * mm});
            skSolve(sketch);
        }
        {
            var Q0;
            Q0=makeQuery(id+"F16.imprint","IMPRINT",FACE,{"disambiguationData":[TD([[makeQuery(id+"F16.imprint","IMPRINT",EDGE,{"derivedFrom":makeQuery(id+"F1.opExtrude","CAP_EDGE",EDGE,{"disambiguationData":[OSD([sQuery(id+"F0.wireOp",EDGE,"E1.left")])],"isStart":true})}),-1.0]])]});
            var Q1;
            {var subQ0=sQuery(id+"F16.wireOp",EDGE,"E79");Q1=makeQuery(id+"F16.imprint","IMPRINT",FACE,{"disambiguationData":[TD([[makeQuery(id+"F16.imprint","IMPRINT",EDGE,{"derivedFrom":subQ0}),-1.0]])]});}
            var Q2;
            Q2=makeQuery(id+"F16.imprint","IMPRINT",FACE,{"disambiguationData":[TD([[makeQuery(id+"F16.imprint","IMPRINT",EDGE,{"derivedFrom":sQuery(id+"F16.wireOp",EDGE,"E87.MirrorCS")}),-1.0]])]});
            extrude(context, id + "F17", {"entities" : qUnion([Q0, Q1, Q2]), "operationType" : NewBodyOperationType.ADD, "depth" : 25 * mm, "offsetDistance" : 25 * mm});
        }
    });
